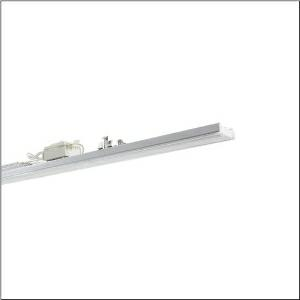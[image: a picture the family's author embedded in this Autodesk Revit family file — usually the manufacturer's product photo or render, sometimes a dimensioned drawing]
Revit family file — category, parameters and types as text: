
# Revit family: licross_21_recessed_mo_52tl12dn4axg3s4
name_source: partatom
category: Lighting Fixtures
units: mm (PartAtom-declared; Revit-internal decimal feet)

## family parameters
Cut with Voids When Loaded = No
Host = Face
Light Source = No
Part Type = Normal
Room Calculation Point = No
Round Connector Dimension = Use Diameter
Shared = No

## types (1)
- --- (1 x LED, 950 lm, 6.7 W, 4000K)
    Apparent Load = 7 VA
    CIE Flux Codes = 72 92 99 100 100
    Color Rendering = 80
    Color Temperature = 4000K
    Default Elevation = 1800 mm
    Description = Licross 21 Recessed MO, luminaire insert, of sheet steel, galvanised, coil coated, white, length: 1.500mm, width: 66mm, height: 67mm, LED rated luminous flux: 10.280lm, light colour: 840, SDCM (Standard Deviation of Colour Matching)MacAdam ≤ 3 SDCM (initial), control gear: DALI 2, with plug, 6-pole, with phase selection, for trunking rail, 9 or 11-core, mains connection: 220..240V, AC, 50/60Hz, rated input power: 62W, for trunking rail, 9-/11-core, internal wiring halogen-free, for emergency light function, converter,control gear: single battery element, battery: LiFePO4, 9Ah, primary optical cover: cover, of PMMA, light emission: direct distribution, primary light characteristic: symmetric, protection rating (complete): IP40, insulation class (complete): insulation class I (protective earthing), certification: CE, UKCA, protection symbol: D if used in an environment without relevant dust loads with corresponding accessories, impact resistance: IK06, permissible ambient temperature for indoor applications: +5..+35°C, standard: EN 60598-2-22, LABS conformity tested according to VDMA 24364:2018-05, reducing of maximum allowable ambient temperature of 5°C with ceiling mounting, corresponds to IFS (International Featured Standards) requirements for safety and quality in the food industry, The light source and the operating device comply with the requirements of the Ecodesign Regulation (EU) 2019/2020 and are replaceable in accordance with this regulation, packaging unit: 1 piece
    Height = 58 mm
    Lamp = 1 x LED
    Lamp Light Flux = 950 lm
    Lamp Power = 6.7 W
    Lamp count = 1
    Length = 1500 mm
    Luminous efficacy = 142 lm/W
    Manufacturer = Siteco
    ModVariant = No
    Model = 52TL12DN4AXG3S4
    Mounting Place = Ceiling
    Mounting Type = Pendant
    Number of Poles = 1
    OnlyDefault = Yes
    Power Factor = 1
    Product Name = Licross 21 Recessed MO
    Product group = luminaire insert | ceiling pendant
    ProductGroupID = 901
    Protection Class = Protection class I
    Protection Degree = IP 40
    RLX_Detail_Level = 1
    RLX_Emergency_Light_Flux = 0 lm
    RLX_Emergency_Type = 0
    RLX_Emergency_Type_DB = No
    RlxData = <blob elided: 25285 chars, md5=1f15bc5c>
    Socket = socket
    Standby Power = 0 W
    System Light Flux = 950 lm
    System Power = 7 W
    Type Comments = : emergency light operation: 3 h
    Type Image = l_1296930.jpg
    URL = http://relux.com
    VarID = @adj_109999
    Voltage = 0 V
    Weight = 0.00 kg
    Width = 66 mm

## geometry (parser evidence)
native form markers: Blend x4, Sweep x11
no freeform markers — native parametric forms only
